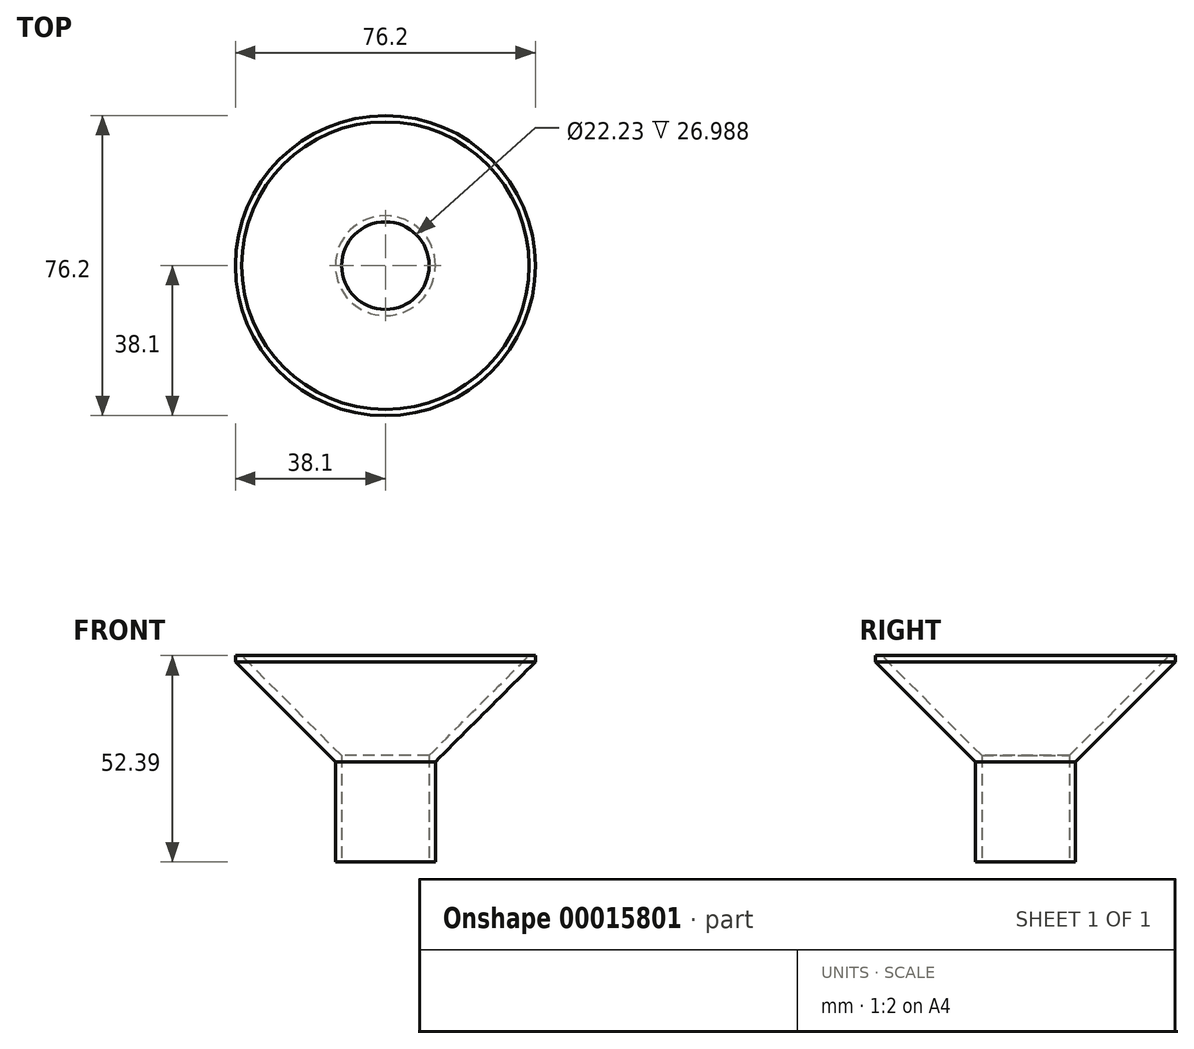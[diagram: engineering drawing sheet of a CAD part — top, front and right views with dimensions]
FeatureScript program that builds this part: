
annotation { "Feature Type Name" : "Feature", "Feature Type Description" : "" }
export const myFeature = defineFeature(function(context is Context, id is Id, definition is map)
    precondition{}
    {
        {
            var Q0;
            Q0=qCreatedBy(makeId("Top.planeOp"),FACE);
            var sketch = newSketch(context, id + "F0", { "sketchPlane" : qUnion([Q0])});
            skCircle(sketch, "E0", {"center": v(0, 0) * mm, "radius": 11.11 * mm});
            skCircle(sketch, "E1", {"center": v(0, 0) * mm, "radius": 38.1 * mm});
            skSolve(sketch);
        }
        {
            var Q0;
            Q0 = qSketchRegion(id + "F0", true);
            extrude(context, id + "F1", {"entities" : qUnion([Q0]), "depth" : 26.99 * mm});
        }
        {
            var Q0;
            Q0=makeQuery(id+"F1.opExtrude","CAP_EDGE",EDGE,{"disambiguationData":[OSD([sQuery(id+"F0.wireOp",EDGE,"E0")])],"isStart":false});
            chamfer(context, id + "F2", {"entities" : qUnion([Q0]), "width" : 25.4 * mm, "tangentPropagation" : true});
        }
        {
            var Q0;
            Q0=makeQuery(id+"F1.opExtrude","CAP_EDGE",EDGE,{"disambiguationData":[OSD([sQuery(id+"F0.wireOp",EDGE,"E1")])],"isStart":true});
            chamfer(context, id + "F3", {"entities" : qUnion([Q0]), "width" : 25.4 * mm, "tangentPropagation" : true});
        }
        {
            var Q0;
            Q0=makeQuery(id+"F1.opExtrude","CAP_FACE",FACE,{"disambiguationData":[OSD([sQuery(id+"F0.wireOp",EDGE,"E0"),sQuery(id+"F0.wireOp",EDGE,"E1")])],"isStart":true});
            extrude(context, id + "F4", {"entities" : qUnion([Q0]), "operationType" : NewBodyOperationType.ADD, "depth" : 25.4 * mm});
        }
    });
